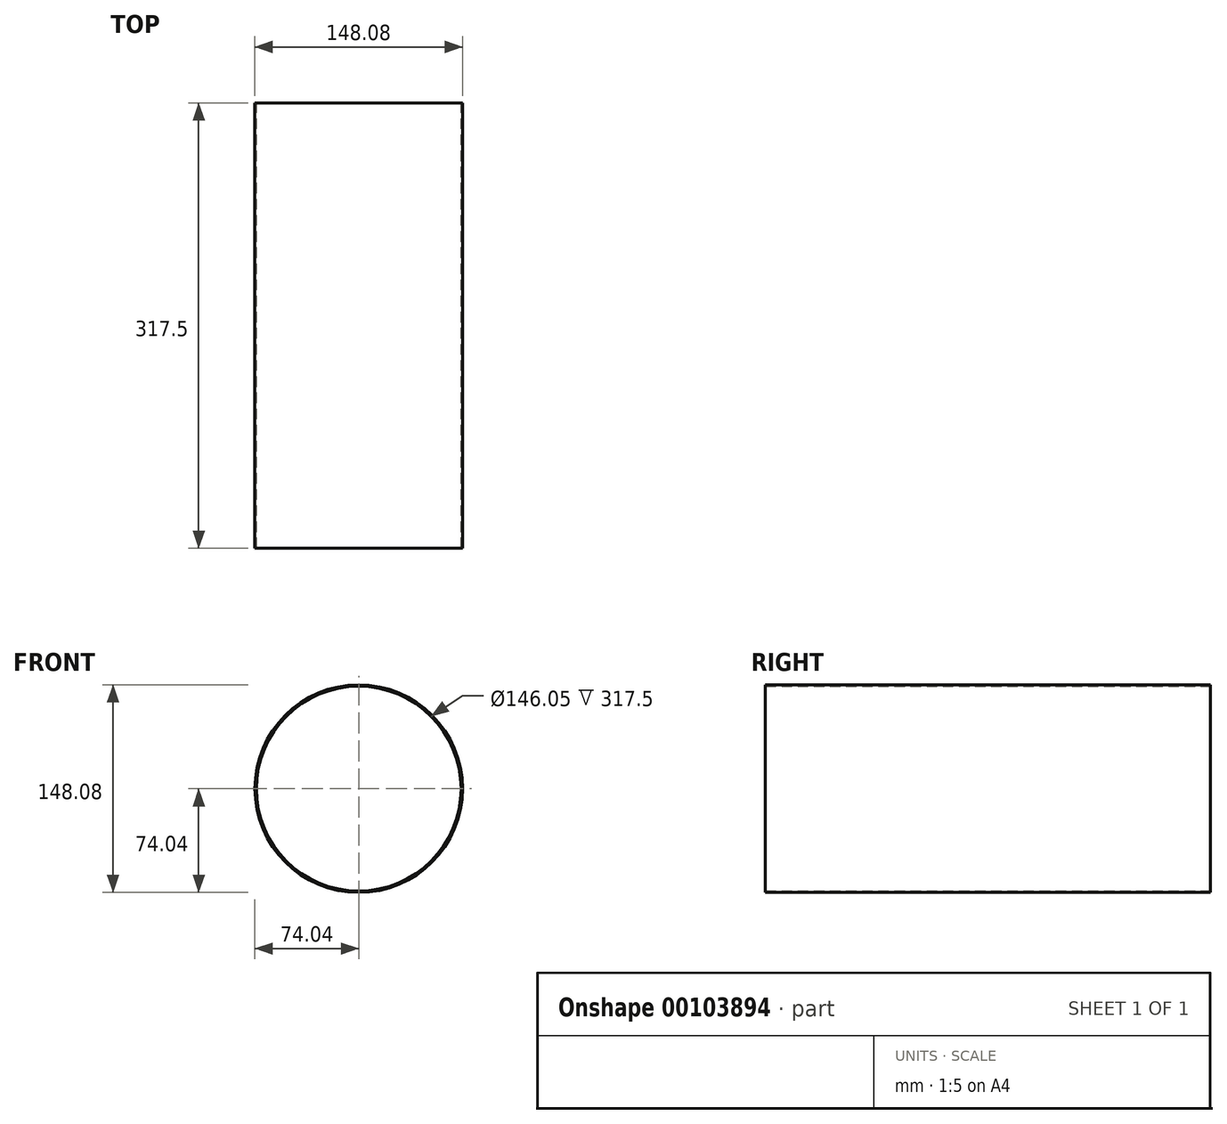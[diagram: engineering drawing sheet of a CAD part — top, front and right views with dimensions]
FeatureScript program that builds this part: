
annotation { "Feature Type Name" : "Feature", "Feature Type Description" : "" }
export const myFeature = defineFeature(function(context is Context, id is Id, definition is map)
    precondition{}
    {
        {
            var Q0;
            Q0=qCreatedBy(makeId("Front.planeOp"),FACE);
            var sketch = newSketch(context, id + "F0", { "sketchPlane" : qUnion([Q0])});
            skCircle(sketch, "E0", {"center": v(0, 0) * mm, "radius": 74.04 * mm});
            skCircle(sketch, "E1", {"center": v(0, 0) * mm, "radius": 73.03 * mm});
            skSolve(sketch);
        }
        {
            var Q0;
            Q0=makeQuery(id+"F0.imprint","IMPRINT",FACE,{"disambiguationData":[TD([[makeQuery(id+"F0.imprint","IMPRINT",EDGE,{"derivedFrom":sQuery(id+"F0.wireOp",EDGE,"E0")}),-1.0]])]});
            var Q1;
            Q1=makeQuery(id+"F0.imprint","IMPRINT",FACE,{"disambiguationData":[TD([[makeQuery(id+"F0.imprint","IMPRINT",EDGE,{"derivedFrom":sQuery(id+"F0.wireOp",EDGE,"E0")}),1.0]])]});
            extrude(context, id + "F1", {"entities" : qUnion([Q0, Q1]), "depth" : 317.5 * mm});
        }
    });
